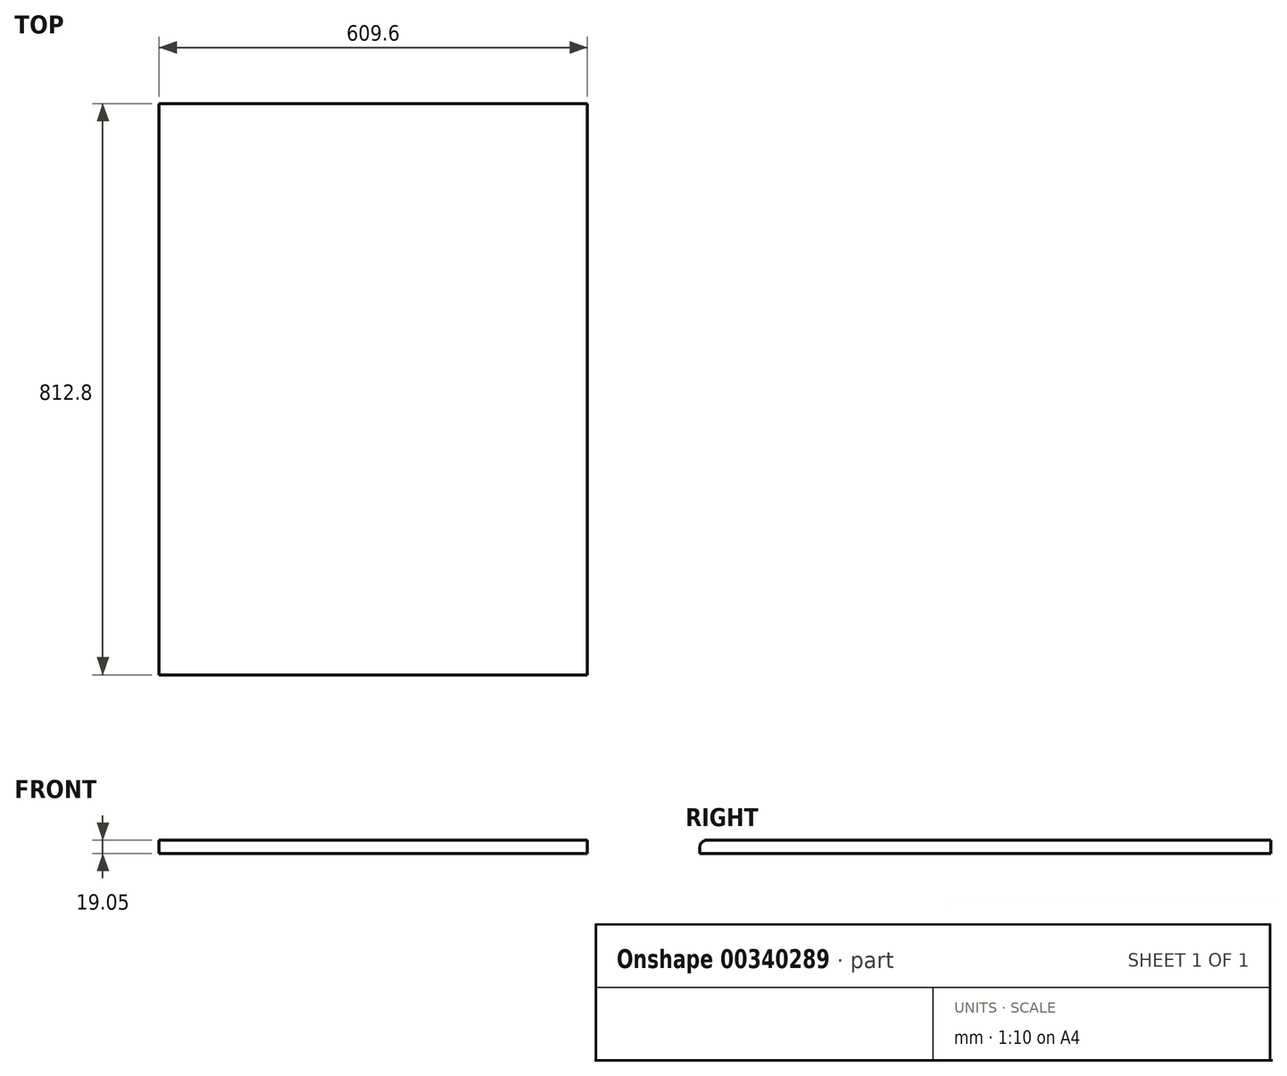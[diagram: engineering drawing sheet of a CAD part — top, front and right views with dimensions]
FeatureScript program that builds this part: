
annotation { "Feature Type Name" : "Feature", "Feature Type Description" : "" }
export const myFeature = defineFeature(function(context is Context, id is Id, definition is map)
    precondition{}
    {
        {
            var Q0;
            Q0=qCreatedBy(makeId("Top.planeOp"),FACE);
            var sketch = newSketch(context, id + "F0", { "sketchPlane" : qUnion([Q0])});
            skLineSegment(sketch, "E0.bottom", {"start": v(304.8, -406.4) * mm, "end": v(-304.8, -406.4) * mm});
            skLineSegment(sketch, "E0.top", {"start": v(304.8, 406.4) * mm, "end": v(-304.8, 406.4) * mm});
            skLineSegment(sketch, "E0.left", {"start": v(304.8, -406.4) * mm, "end": v(304.8, 406.4) * mm});
            skLineSegment(sketch, "E0.right", {"start": v(-304.8, -406.4) * mm, "end": v(-304.8, 406.4) * mm});
            skPoint(sketch, "E0.middle", {"position": v(0, 0) * mm});
            skSolve(sketch);
        }
        {
            var Q0;
            Q0 = qSketchRegion(id + "F0", true);
            extrude(context, id + "F1", {"entities" : qUnion([Q0]), "depth" : 19.05 * mm});
        }
        {
            var Q0;
            Q0=makeQuery(id+"F1.opExtrude","CAP_EDGE",EDGE,{"disambiguationData":[OSD([sQuery(id+"F0.wireOp",EDGE,"E0.bottom")])],"isStart":false});
            fillet(context, id + "F2", {"entities" : qUnion([Q0]), "radius" : 10.16 * mm, "tangentPropagation" : true, "allowEdgeOverflow" : false});
        }
    });
